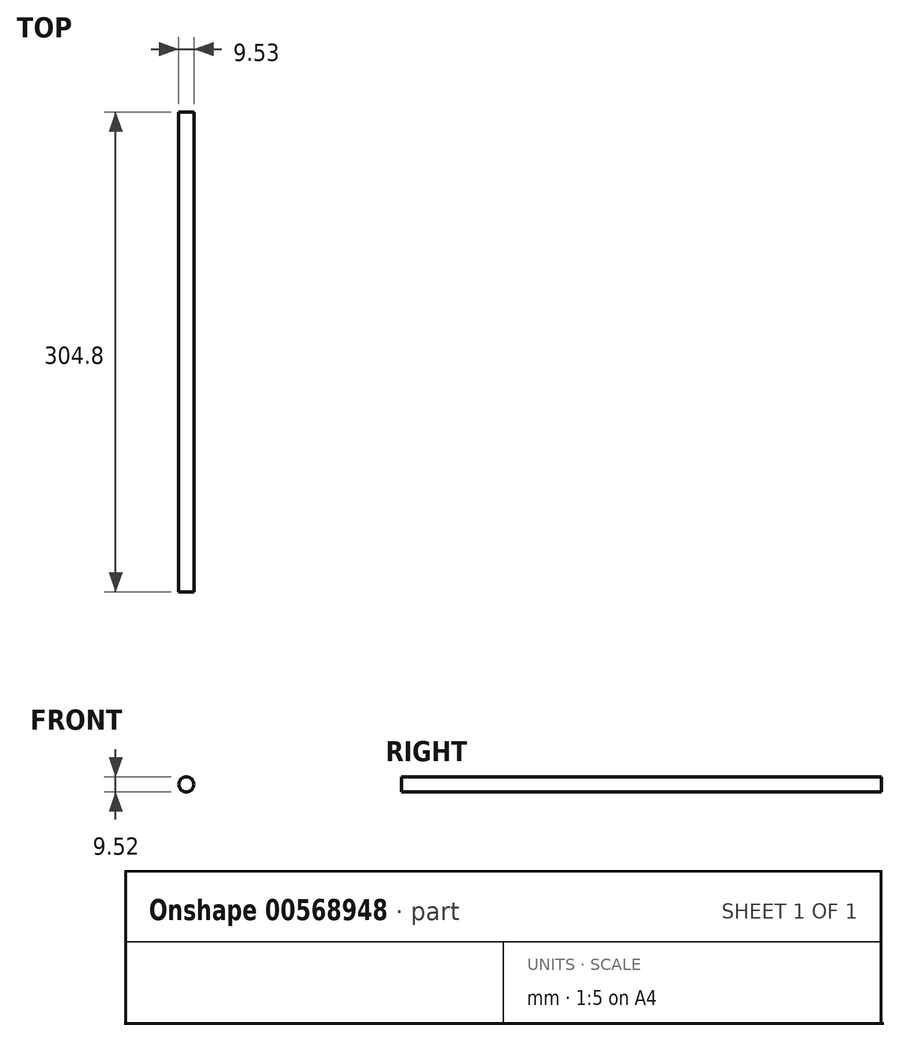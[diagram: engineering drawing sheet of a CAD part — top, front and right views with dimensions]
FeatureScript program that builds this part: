
annotation { "Feature Type Name" : "Feature", "Feature Type Description" : "" }
export const myFeature = defineFeature(function(context is Context, id is Id, definition is map)
    precondition{}
    {
        {
            var Q0;
            Q0=qCreatedBy(makeId("Front.planeOp"),FACE);
            var sketch = newSketch(context, id + "F0", { "sketchPlane" : qUnion([Q0])});
            skCircle(sketch, "E0", {"center": v(-40.97, 26.5) * mm, "radius": 4.76 * mm});
            skSolve(sketch);
        }
        {
            var Q0;
            Q0 = qSketchRegion(id + "F0", true);
            extrude(context, id + "F1", {"entities" : qUnion([Q0]), "depth" : 304.8 * mm, "offsetDistance" : 25.4 * mm});
        }
    });
